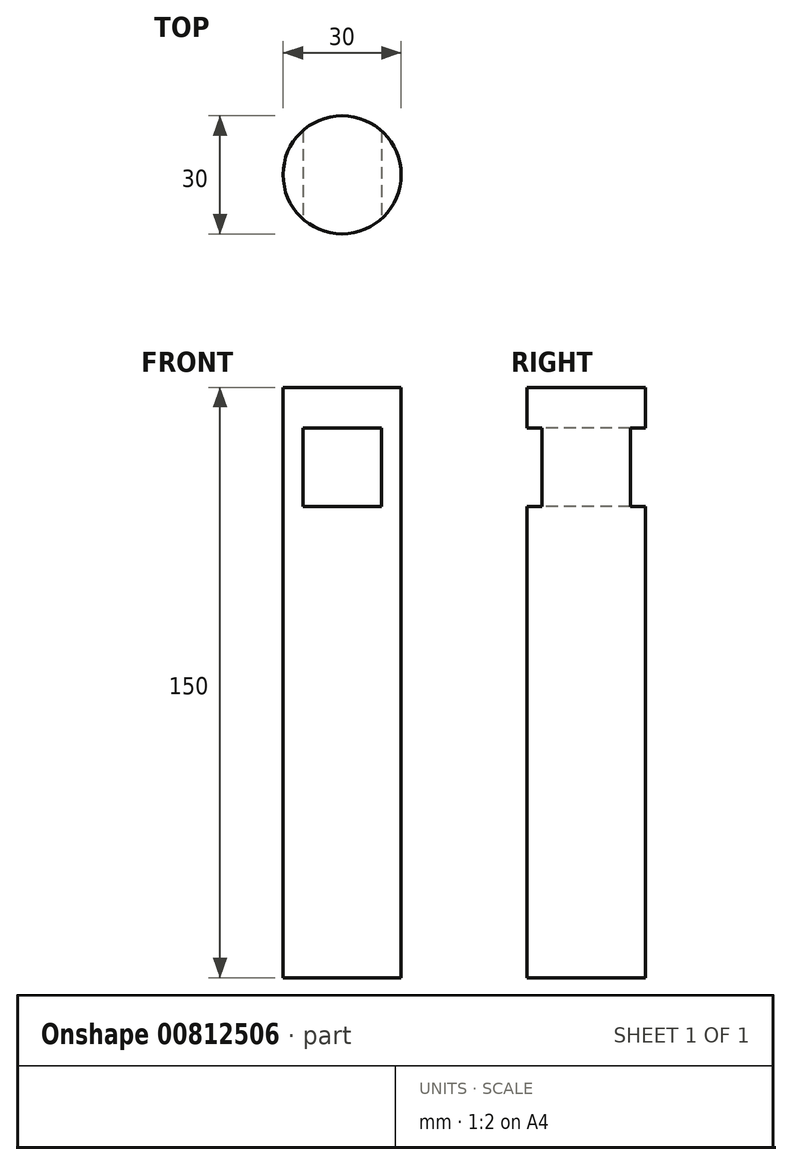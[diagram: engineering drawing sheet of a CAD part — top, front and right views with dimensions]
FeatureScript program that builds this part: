
annotation { "Feature Type Name" : "Feature", "Feature Type Description" : "" }
export const myFeature = defineFeature(function(context is Context, id is Id, definition is map)
    precondition{}
    {
        {
            var Q0;
            Q0=qCreatedBy(makeId("Top.planeOp"),FACE);
            var sketch = newSketch(context, id + "F0", { "sketchPlane" : qUnion([Q0])});
            skCircle(sketch, "E0", {"center": v(0, 0) * mm, "radius": 15 * mm});
            skSolve(sketch);
        }
        {
            var Q0;
            Q0=makeQuery(id+"F0.imprint","IMPRINT",FACE,{"disambiguationData":[TD([[makeQuery(id+"F0.imprint","IMPRINT",EDGE,{"derivedFrom":sQuery(id+"F0.wireOp",EDGE,"E0")}),1.0]])]});
            var Q1;
            Q1=sQuery(id+"F0.wireOp",EDGE,"E0");
            extrude(context, id + "F1", {"entities" : qUnion([Q0]), "surfaceEntities" : qUnion([Q1]), "depth" : 150 * mm, "offsetDistance" : 25 * mm});
        }
        {
            var Q0;
            Q0=qCreatedBy(makeId("Front.planeOp"),FACE);
            var sketch = newSketch(context, id + "F2", { "sketchPlane" : qUnion([Q0])});
            skLineSegment(sketch, "E1.bottom", {"start": v(10, 119.67) * mm, "end": v(-10, 119.67) * mm});
            skLineSegment(sketch, "E1.top", {"start": v(10, 139.67) * mm, "end": v(-10, 139.67) * mm});
            skLineSegment(sketch, "E1.left", {"start": v(10, 119.67) * mm, "end": v(10, 139.67) * mm});
            skLineSegment(sketch, "E1.right", {"start": v(-10, 119.67) * mm, "end": v(-10, 139.67) * mm});
            skPoint(sketch, "E1.middle", {"position": v(0, 129.67) * mm});
            skSolve(sketch);
        }
        {
            var Q0;
            Q0 = qSketchRegion(id + "F2", true);
            extrude(context, id + "F3", {"entities" : qUnion([Q0]), "operationType" : NewBodyOperationType.REMOVE, "oppositeDirection" : true, "depth" : 25 * mm, "offsetDistance" : 25 * mm, "hasSecondDirection" : true, "secondDirectionOppositeDirection" : false, "secondDirectionDepth" : 25 * mm});
        }
    });
